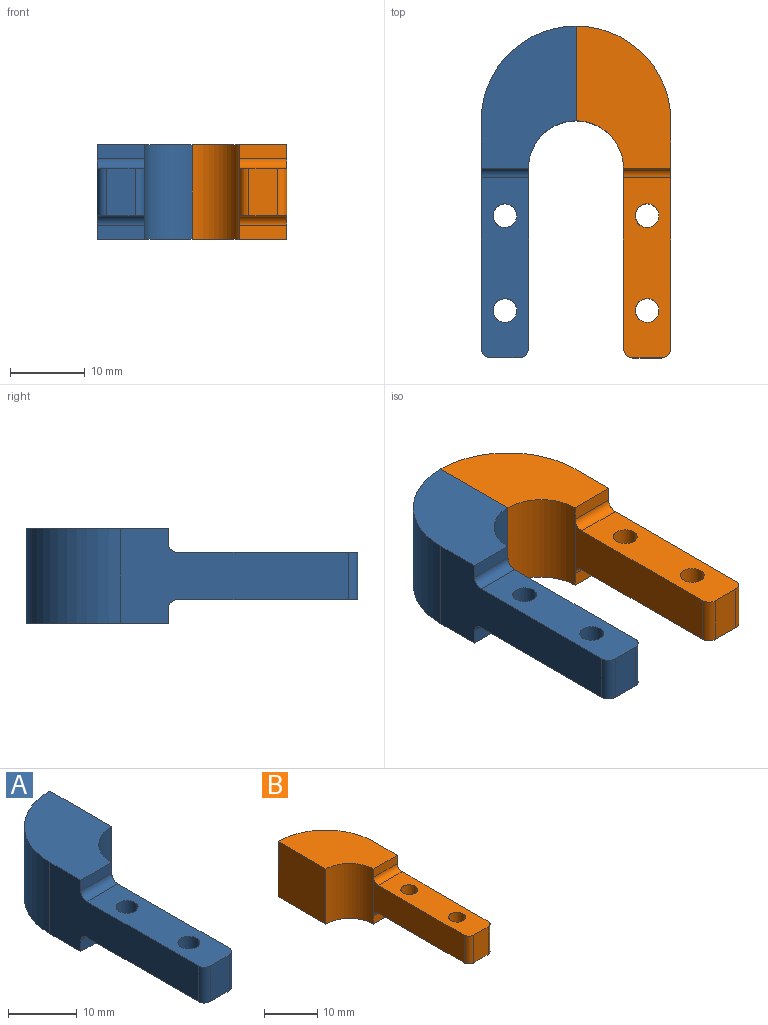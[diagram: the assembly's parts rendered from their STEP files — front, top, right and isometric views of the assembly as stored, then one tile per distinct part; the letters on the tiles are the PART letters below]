
ASSEMBLY  parts=2 mates=1
PART A: 18 faces, bbox 12.7x44.5x12.7 mm
  f0: plane 30.48x12.7mm, normal (-1,0,0), area 234.6mm2, adj f3,f4,f6,f8,f9,f10,f11,f12
  f1: plane 6.35x3.81mm, normal (0,-1,0), area 24.2mm2, adj f8,f10,f14,f15
  f2: plane 24.13x8.89mm, normal (1,0,0), area 153.9mm2, adj f7,f8,f10,f12,f13,f15
  f3: plane 19.05x12.7mm, normal (0,0,1), area 175.7mm2, adj f0,f5,f6,f7,f11
  f4: plane 19.05x12.7mm, normal (0,0,-1), area 175.7mm2, adj f0,f5,f6,f7,f9
  f5: plane 12.7x12.7mm, normal (1,0,0), area 161.3mm2, adj f3,f4,f6,f7
  f6: cylinder r=12.7mm len=12.7mm, axis (0,0,-1), area 253.4mm2, adj f0,f3,f4,f5
  f7: cylinder r=6.35mm len=12.7mm, axis (0,0,-1), area 126.7mm2, adj f2,f3,f4,f5,f9,f11
  f8: plane 24.13x6.35mm, normal (0,0,-1), area 136.7mm2, adj f0,f1,f2,f12,f14,f15,f16,f17
  f9: plane 6.35x1.91mm, normal (0,-1,0), area 12.1mm2, adj f0,f4,f7,f12
  f10: plane 24.13x6.35mm, normal (0,0,1), area 136.7mm2, adj f0,f1,f2,f13,f14,f15,f16,f17
  f11: plane 6.35x1.91mm, normal (0,-1,0), area 12.1mm2, adj f0,f3,f7,f13
  f12: cylinder r=1.27mm len=6.35mm, axis (-1,0,0), area 12.7mm2, adj f0,f2,f8,f9
  f13: cylinder r=1.27mm len=6.35mm, axis (1,0,0), area 12.7mm2, adj f0,f2,f10,f11
  f14: cylinder r=1.27mm len=6.35mm, axis (0,0,-1), area 12.7mm2, adj f0,f1,f8,f10
  f15: cylinder r=1.27mm len=6.35mm, axis (0,0,-1), area 12.7mm2, adj f1,f2,f8,f10
  f16: cylinder r=1.59mm len=6.35mm, axis (0,0,1), area 63.3mm2, adj f8,f10
  f17: cylinder r=1.59mm len=6.35mm, axis (0,0,1), area 63.3mm2, adj f8,f10
PART B: 18 faces, bbox 12.7x44.5x12.7 mm
  f0: plane 6.35x3.81mm, normal (0,-1,0), area 24.2mm2, adj f8,f10,f14,f15
  f1: plane 30.48x12.7mm, normal (1,0,0), area 234.6mm2, adj f3,f4,f5,f8,f9,f10,f11,f12
  f2: plane 24.13x8.89mm, normal (-1,0,0), area 153.9mm2, adj f7,f8,f10,f12,f13,f14
  f3: plane 19.05x12.7mm, normal (0,0,1), area 175.7mm2, adj f1,f5,f6,f7,f11
  f4: plane 19.05x12.7mm, normal (0,0,-1), area 175.7mm2, adj f1,f5,f6,f7,f9
  f5: cylinder r=12.7mm len=12.7mm, axis (0,0,-1), area 253.4mm2, adj f1,f3,f4,f6
  f6: plane 12.7x12.7mm, normal (-1,0,0), area 161.3mm2, adj f3,f4,f5,f7
  f7: cylinder r=6.35mm len=12.7mm, axis (0,0,-1), area 126.7mm2, adj f2,f3,f4,f6,f9,f11
  f8: plane 24.13x6.35mm, normal (0,0,-1), area 136.7mm2, adj f0,f1,f2,f12,f14,f15,f16,f17
  f9: plane 6.35x1.91mm, normal (0,-1,0), area 12.1mm2, adj f1,f4,f7,f12
  f10: plane 24.13x6.35mm, normal (0,0,1), area 136.7mm2, adj f0,f1,f2,f13,f14,f15,f16,f17
  f11: plane 6.35x1.91mm, normal (0,-1,0), area 12.1mm2, adj f1,f3,f7,f13
  f12: cylinder r=1.27mm len=6.35mm, axis (-1,0,0), area 12.7mm2, adj f1,f2,f8,f9
  f13: cylinder r=1.27mm len=6.35mm, axis (1,0,0), area 12.7mm2, adj f1,f2,f10,f11
  f14: cylinder r=1.27mm len=6.35mm, axis (0,0,-1), area 12.7mm2, adj f0,f2,f8,f10
  f15: cylinder r=1.27mm len=6.35mm, axis (0,0,-1), area 12.7mm2, adj f0,f1,f8,f10
  f16: cylinder r=1.59mm len=6.35mm, axis (0,0,1), area 63.3mm2, adj f8,f10
  f17: cylinder r=1.59mm len=6.35mm, axis (0,0,1), area 63.3mm2, adj f8,f10
PLACE A t=(15.02,-2.9,0.23)mm
PLACE B t=(-10.38,-2.9,0.23)mm
MATE planar A.f3 <-> B.f3  axis (0,0,1) through (2.32,35.2,6.58)mm
